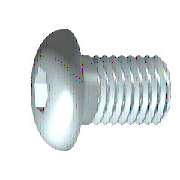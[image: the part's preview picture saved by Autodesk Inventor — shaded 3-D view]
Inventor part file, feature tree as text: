
AUTODESK INVENTOR PART (.ipt)
format: ipt  version: 2013 (Build 170138000, 138)  size: 185,344 bytes
history: native  units: mm (DEFAULTED — no unit token found)
features: sketch x2, extrude x1, plane x1, fillet x1
ambient origin geometry x7: Origin, YZ Plane, XY Plane, X Axis, Y Axis, Z Axis, Center Point
bodies: Solid1 (feature_tree), Body (feature_tree)
feature tree (5):
  extrude  "Slot"  Depth=1.59014mm
  plane  "Work Plane1"
  fillet  "Fillet2"  Radius=2.2098mm
  sketch  "Sketch1"  dims[d1=23.80976mm d2=1.59014mm d3=2.2098mm]
  sketch  "Sketch2"  dims[d4=1.3208mm d5=60.0deg d6=4.1656mm d7=4.1656mm d8=2.756963mm d9=7.9248mm d10=90.0deg d11=10.0mm d12=0.0mm d13=23.80976mm d14=0.0mm d15=0.486918mm d16=0.486918mm d17=1.9558mm d19=0.0mm d26=25.4mm d27=45.0deg d28=0.0mm d29=0.0mm d30=0.1mm]
